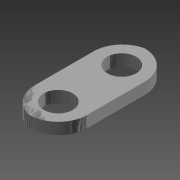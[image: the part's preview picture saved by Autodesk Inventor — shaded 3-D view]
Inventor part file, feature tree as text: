
AUTODESK INVENTOR PART (.ipt)
format: ipt  version: 2015 (Build 190159000, 159)  size: 103,936 bytes
history: native  units: mm
features: other x3, sketch x2, hole x1, fillet x1
ambient origin geometry x8: Origin, YZ Plane, XZ Plane, XY Plane, X Axis, Y Axis, Z Axis, Center Point
bodies: Body1 (feature_tree)
feature tree (7):
  other  "Bryła1"
  other  "Powierzchnia1"
  hole  "Otwór1"  [1 undecoded]
  fillet  "Zaokrąglenie1"  Radius=9.0mm
  sketch  "Szkic1"
  other  "Płyta1"
  sketch  "Szkic2"
note: 1 required parameter value undecoded (feature->parameter linkage not recoverable at this tier; creation-order binding heuristic only, values carry confidence <= 0.55)
